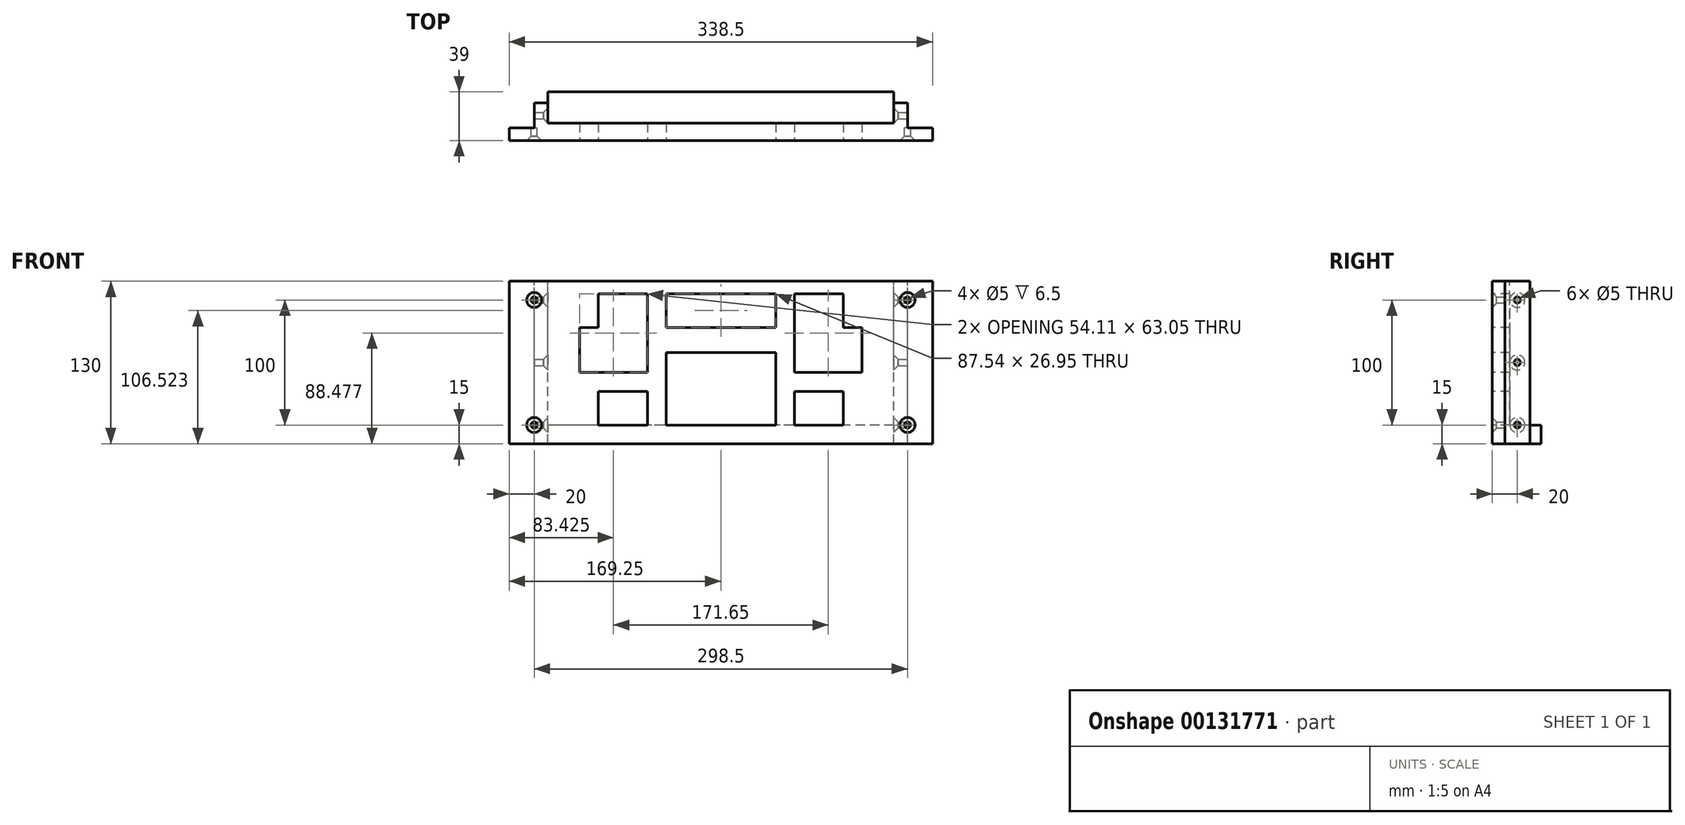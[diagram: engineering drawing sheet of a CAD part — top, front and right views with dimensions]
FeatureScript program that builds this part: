
annotation { "Feature Type Name" : "Feature", "Feature Type Description" : "" }
export const myFeature = defineFeature(function(context is Context, id is Id, definition is map)
    precondition{}
    {
        {
            var Q0;
            Q0=qCreatedBy(makeId("Front.planeOp"),FACE);
            var sketch = newSketch(context, id + "F0", { "sketchPlane" : qUnion([Q0])});
            skLineSegment(sketch, "E0.bottom", {"start": v(0, 0) * mm, "end": v(298.5, 0) * mm});
            skLineSegment(sketch, "E0.top", {"start": v(0, 130) * mm, "end": v(298.5, 130) * mm});
            skLineSegment(sketch, "E0.left", {"start": v(0, 0) * mm, "end": v(0, 130) * mm});
            skLineSegment(sketch, "E0.right", {"start": v(298.5, 0) * mm, "end": v(298.5, 130) * mm});
            skSolve(sketch);
        }
        {
            var Q0;
            Q0=makeQuery(id+"F0.imprint","IMPRINT",FACE,{"disambiguationData":[TD([[makeQuery(id+"F0.imprint","IMPRINT",EDGE,{"derivedFrom":sQuery(id+"F0.wireOp",EDGE,"E0.bottom")}),1.0]])]});
            extrude(context, id + "F1", {"entities" : qUnion([Q0]), "depth" : 14 * mm});
        }
        {
            var Q0;
            Q0=makeQuery(id+"F1.opExtrude","SWEPT_FACE",FACE,{"disambiguationData":[OSD([sQuery(id+"F0.wireOp",EDGE,"E0.top")])]});
            var sketch = newSketch(context, id + "F2", { "sketchPlane" : qUnion([Q0])});
            skLineSegment(sketch, "E1", {"start": v(0, -14) * mm, "end": v(-20, -14) * mm});
            skLineSegment(sketch, "E2", {"start": v(-20, -14) * mm, "end": v(-20, -4) * mm});
            skLineSegment(sketch, "E3", {"start": v(-20, -4) * mm, "end": v(0, -4) * mm});
            skLineSegment(sketch, "E4", {"start": v(0, -4) * mm, "end": v(0, -14) * mm});
            skLineSegment(sketch, "E5.bottom", {"start": v(298.5, -14) * mm, "end": v(318.5, -14) * mm});
            skLineSegment(sketch, "E5.top", {"start": v(298.5, -4) * mm, "end": v(318.5, -4) * mm});
            skLineSegment(sketch, "E5.left", {"start": v(298.5, -14) * mm, "end": v(298.5, -4) * mm});
            skLineSegment(sketch, "E6", {"start": v(318.5, -4) * mm, "end": v(318.5, -14) * mm});
            skSolve(sketch);
        }
        {
            var Q0;
            Q0=makeQuery(id+"F2.imprint","IMPRINT",FACE,{"disambiguationData":[TD([[makeQuery(id+"F2.imprint","IMPRINT",EDGE,{"derivedFrom":sQuery(id+"F2.wireOp",EDGE,"E5.bottom")}),1.0]])]});
            var Q1;
            Q1=makeQuery(id+"F2.imprint","IMPRINT",FACE,{"disambiguationData":[TD([[makeQuery(id+"F2.imprint","IMPRINT",EDGE,{"derivedFrom":sQuery(id+"F2.wireOp",EDGE,"E1")}),-1.0]])]});
            var Q2;
            Q2=makeQuery(id+"F2.imprint","IMPRINT",FACE,{"disambiguationData":[TD([[makeQuery(id+"F2.imprint","IMPRINT",EDGE,{"derivedFrom":sQuery(id+"F2.wireOp",EDGE,"RW2Kzl6v-dZsG-AqaK-MO7M-Wq128sQEg4HD.bottom")}),-1.0]])]});
            var Q3;
            Q3=makeQuery(id+"F1.opExtrude","SWEPT_FACE",FACE,{"disambiguationData":[OSD([sQuery(id+"F0.wireOp",EDGE,"E0.bottom")])]});
            extrude(context, id + "F3", {"entities" : qUnion([Q0, Q1, Q2]), "operationType" : NewBodyOperationType.ADD, "endBound" : BoundingType.UP_TO_SURFACE, "oppositeDirection" : true, "endBoundEntityFace" : qUnion([Q3]), "depth" : 25 * mm});
        }
        {
            var Q0;
            Q0=makeQuery(id+"F3.boolean.opBoolean","MERGE",FACE,{"derivedFrom":[makeQuery(id+"F1.opExtrude","SWEPT_FACE",FACE,{"disambiguationData":[OSD([sQuery(id+"F0.wireOp",EDGE,"E0.top")])]}),makeQuery(id+"F3.opExtrude","CAP_FACE",FACE,{"disambiguationData":[OSD([sQuery(id+"F2.wireOp",EDGE,"E1"),sQuery(id+"F2.wireOp",EDGE,"E2"),sQuery(id+"F2.wireOp",EDGE,"E3"),sQuery(id+"F2.wireOp",EDGE,"E4")])],"isStart":true}),makeQuery(id+"F3.opExtrude","CAP_FACE",FACE,{"disambiguationData":[OSD([sQuery(id+"F2.wireOp",EDGE,"E5.bottom"),sQuery(id+"F2.wireOp",EDGE,"E5.top"),sQuery(id+"F2.wireOp",EDGE,"E5.left"),sQuery(id+"F2.wireOp",EDGE,"E5.right")])],"isStart":true})]});
            var sketch = newSketch(context, id + "F4", { "sketchPlane" : qUnion([Q0])});
            skLineSegment(sketch, "E7", {"start": v(0, 0) * mm, "end": v(0, 16) * mm});
            skLineSegment(sketch, "E8", {"start": v(0, 16) * mm, "end": v(11, 16) * mm});
            skLineSegment(sketch, "E9", {"start": v(11, 16) * mm, "end": v(11, 0) * mm});
            skLineSegment(sketch, "E10", {"start": v(11, 0) * mm, "end": v(0, 0) * mm});
            skLineSegment(sketch, "E11.bottom", {"start": v(298.5, 0) * mm, "end": v(287.5, 0) * mm});
            skLineSegment(sketch, "E11.top", {"start": v(298.5, 16) * mm, "end": v(287.5, 16) * mm});
            skLineSegment(sketch, "E11.left", {"start": v(298.5, 0) * mm, "end": v(298.5, 16) * mm});
            skLineSegment(sketch, "E11.right", {"start": v(287.5, 0) * mm, "end": v(287.5, 16) * mm});
            skSolve(sketch);
        }
        {
            var Q0;
            Q0=makeQuery(id+"F4.imprint","IMPRINT",FACE,{"disambiguationData":[TD([[makeQuery(id+"F4.imprint","IMPRINT",EDGE,{"derivedFrom":sQuery(id+"F4.wireOp",EDGE,"g1681GE8-kr8q-vAWY-LNZA-GesWc0OhcODc.bottom")}),1.0]])]});
            var Q1;
            Q1=makeQuery(id+"F4.imprint","IMPRINT",FACE,{"disambiguationData":[TD([[makeQuery(id+"F4.imprint","IMPRINT",EDGE,{"derivedFrom":sQuery(id+"F4.wireOp",EDGE,"E7")}),-1.0]])]});
            var Q2;
            Q2=makeQuery(id+"F4.imprint","IMPRINT",FACE,{"disambiguationData":[TD([[makeQuery(id+"F4.imprint","IMPRINT",EDGE,{"derivedFrom":sQuery(id+"F4.wireOp",EDGE,"E11.bottom")}),1.0]])]});
            var Q3;
            {var subQ0=sQuery(id+"F0.wireOp",EDGE,"E0.bottom");Q3=makeQuery(id+"F3.boolean.opBoolean","MERGE",FACE,{"derivedFrom":[makeQuery(id+"F1.opExtrude","SWEPT_FACE",FACE,{"disambiguationData":[OSD([subQ0])]}),makeQuery(id+"F3.opExtrude","CAP_FACE",FACE,{"disambiguationData":[OSD([subQ0]),ownerDisambiguation([makeQuery(id+"F3.opExtrude","SWEPT_BODY",BODY,{"disambiguationData":[OSD([sQuery(id+"F2.wireOp",EDGE,"E1"),sQuery(id+"F2.wireOp",EDGE,"E2"),sQuery(id+"F2.wireOp",EDGE,"E3"),sQuery(id+"F2.wireOp",EDGE,"E4")])]})])],"isStart":false}),makeQuery(id+"F3.opExtrude","CAP_FACE",FACE,{"disambiguationData":[OSD([subQ0]),ownerDisambiguation([makeQuery(id+"F3.opExtrude","SWEPT_BODY",BODY,{"disambiguationData":[OSD([sQuery(id+"F2.wireOp",EDGE,"E5.bottom"),sQuery(id+"F2.wireOp",EDGE,"E5.top"),sQuery(id+"F2.wireOp",EDGE,"E5.left"),sQuery(id+"F2.wireOp",EDGE,"E5.right")])]})])],"isStart":false})]});}
            extrude(context, id + "F5", {"entities" : qUnion([Q0, Q1, Q2]), "operationType" : NewBodyOperationType.ADD, "endBound" : BoundingType.UP_TO_SURFACE, "oppositeDirection" : true, "endBoundEntityFace" : qUnion([Q3]), "depth" : 25 * mm});
        }
        {
            var Q0;
            Q0=makeQuery(id+"F3.boolean.opBoolean","MERGE",FACE,{"derivedFrom":[makeQuery(id+"F1.opExtrude","CAP_FACE",FACE,{"disambiguationData":[OSD([sQuery(id+"F0.wireOp",EDGE,"E0.bottom"),sQuery(id+"F0.wireOp",EDGE,"E0.top"),sQuery(id+"F0.wireOp",EDGE,"E0.left"),sQuery(id+"F0.wireOp",EDGE,"E0.right")])],"isStart":false}),makeQuery(id+"F3.opExtrude","SWEPT_FACE",FACE,{"disambiguationData":[OSD([sQuery(id+"F2.wireOp",EDGE,"E1")])]}),makeQuery(id+"F3.opExtrude","SWEPT_FACE",FACE,{"disambiguationData":[OSD([sQuery(id+"F2.wireOp",EDGE,"E5.bottom")])]})]});
            var sketch = newSketch(context, id + "F6", { "sketchPlane" : qUnion([Q0])});
            skLineSegment(sketch, "E12.0", {"start": v(51.37, 93.05) * mm, "end": v(51.37, 120) * mm});
            skLineSegment(sketch, "E12.6", {"start": v(51.37, 120) * mm, "end": v(247.13, 120) * mm});
            skLineSegment(sketch, "E12.8", {"start": v(51.37, 15) * mm, "end": v(51.37, 41.95) * mm});
            skLineSegment(sketch, "E12.11", {"start": v(36.37, 93.05) * mm, "end": v(51.37, 93.05) * mm});
            skLineSegment(sketch, "E13", {"start": v(149.25, 120) * mm, "end": v(149.25, 15) * mm});
            skLineSegment(sketch, "E14", {"start": v(51.37, 15) * mm, "end": v(149.25, 120) * mm, "construction": true});
            skLineSegment(sketch, "E15", {"start": v(149.25, 120) * mm, "end": v(247.13, 15) * mm, "construction": true});
            skLineSegment(sketch, "E16.bottom", {"start": v(105.48, 73.05) * mm, "end": v(193.02, 73.05) * mm});
            skLineSegment(sketch, "E16.top", {"start": v(105.48, 15) * mm, "end": v(193.02, 15) * mm});
            skLineSegment(sketch, "E16.left", {"start": v(105.48, 73.05) * mm, "end": v(105.48, 15) * mm});
            skLineSegment(sketch, "E16.right", {"start": v(193.02, 73.05) * mm, "end": v(193.02, 15) * mm});
            skLineSegment(sketch, "E17.bottom", {"start": v(262.13, 56.95) * mm, "end": v(208.02, 56.95) * mm});
            skLineSegment(sketch, "E17.right", {"start": v(208.02, 56.95) * mm, "end": v(208.02, 120) * mm});
            skLineSegment(sketch, "E18.bottom", {"start": v(90.48, 120) * mm, "end": v(51.37, 120) * mm});
            skLineSegment(sketch, "E18.top", {"start": v(90.48, 56.95) * mm, "end": v(36.37, 56.95) * mm});
            skLineSegment(sketch, "E18.left", {"start": v(90.48, 120) * mm, "end": v(90.48, 56.95) * mm});
            skLineSegment(sketch, "E18.right", {"start": v(51.37, 120) * mm, "end": v(51.37, 93.05) * mm});
            skLineSegment(sketch, "E19.bottom", {"start": v(105.48, 120) * mm, "end": v(193.02, 120) * mm});
            skLineSegment(sketch, "E19.top", {"start": v(105.48, 93.05) * mm, "end": v(193.02, 93.05) * mm});
            skLineSegment(sketch, "E19.left", {"start": v(105.48, 120) * mm, "end": v(105.48, 93.05) * mm});
            skLineSegment(sketch, "E19.right", {"start": v(193.02, 120) * mm, "end": v(193.02, 93.05) * mm});
            skLineSegment(sketch, "E20.bottom", {"start": v(208.02, 15) * mm, "end": v(247.13, 15) * mm});
            skLineSegment(sketch, "E20.top", {"start": v(208.02, 41.95) * mm, "end": v(247.13, 41.95) * mm});
            skLineSegment(sketch, "E20.left", {"start": v(208.02, 15) * mm, "end": v(208.02, 41.95) * mm});
            skLineSegment(sketch, "E21.bottom", {"start": v(51.37, 15) * mm, "end": v(90.48, 15) * mm});
            skLineSegment(sketch, "E21.top", {"start": v(51.37, 41.95) * mm, "end": v(90.48, 41.95) * mm});
            skLineSegment(sketch, "E21.right", {"start": v(90.48, 15) * mm, "end": v(90.48, 41.95) * mm});
            skLineSegment(sketch, "E22", {"start": v(36.37, 93.05) * mm, "end": v(36.37, 56.95) * mm});
            skLineSegment(sketch, "E23.trimOffspring", {"start": v(247.13, 15) * mm, "end": v(51.37, 15) * mm});
            skLineSegment(sketch, "E24.trimOffspring", {"start": v(247.13, 120) * mm, "end": v(208.02, 120) * mm});
            skLineSegment(sketch, "E25.0", {"start": v(11, 0) * mm, "end": v(11, 130) * mm});
            skLineSegment(sketch, "E26.0", {"start": v(287.5, 0) * mm, "end": v(287.5, 130) * mm});
            skLineSegment(sketch, "E27", {"start": v(11, 15) * mm, "end": v(90.48, 15) * mm});
            skLineSegment(sketch, "E28", {"start": v(247.13, 93.05) * mm, "end": v(262.13, 93.05) * mm});
            skPoint(sketch, "E28.startSnap0", {"position": v(149.25, 93.05) * mm});
            skLineSegment(sketch, "E29", {"start": v(262.13, 93.05) * mm, "end": v(262.13, 56.95) * mm});
            skLineSegment(sketch, "E30", {"start": v(247.13, 93.05) * mm, "end": v(247.13, 120) * mm});
            skLineSegment(sketch, "E31", {"start": v(247.13, 41.95) * mm, "end": v(247.13, 15) * mm});
            skLineSegment(sketch, "E32.trimOffspring", {"start": v(149.25, 15) * mm, "end": v(287.5, 15) * mm});
            skSolve(sketch);
        }
        {
            var Q0;
            {var subQ0=sQuery(id+"F6.wireOp",EDGE,"E12.11");Q0=makeQuery(id+"F6.imprint","IMPRINT",FACE,{"disambiguationData":[TD([[makeQuery(id+"F6.imprint","IMPRINT",EDGE,{"derivedFrom":subQ0}),-1.0]])]});}
            var Q1;
            Q1=makeQuery(id+"F6.imprint","IMPRINT",FACE,{"disambiguationData":[TD([[makeQuery(id+"F6.imprint","IMPRINT",EDGE,{"derivedFrom":sQuery(id+"F6.wireOp",EDGE,"E21.bottom")}),1.0]])]});
            var Q2;
            {var subQ5=sQuery(id+"F6.wireOp",EDGE,"E16.left");Q2=makeQuery(id+"F6.imprint","IMPRINT",FACE,{"disambiguationData":[TD([[makeQuery(id+"F6.imprint","IMPRINT",EDGE,{"derivedFrom":subQ5}),1.0]])]});}
            var Q3;
            {var subQ5=sQuery(id+"F6.wireOp",EDGE,"E16.right");Q3=makeQuery(id+"F6.imprint","IMPRINT",FACE,{"disambiguationData":[TD([[makeQuery(id+"F6.imprint","IMPRINT",EDGE,{"derivedFrom":subQ5}),-1.0]])]});}
            var Q4;
            {var subQ5=sQuery(id+"F6.wireOp",EDGE,"E19.left");Q4=makeQuery(id+"F6.imprint","IMPRINT",FACE,{"disambiguationData":[TD([[makeQuery(id+"F6.imprint","IMPRINT",EDGE,{"derivedFrom":subQ5}),1.0]])]});}
            var Q5;
            {var subQ5=sQuery(id+"F6.wireOp",EDGE,"E19.right");Q5=makeQuery(id+"F6.imprint","IMPRINT",FACE,{"disambiguationData":[TD([[makeQuery(id+"F6.imprint","IMPRINT",EDGE,{"derivedFrom":subQ5}),-1.0]])]});}
            var Q6;
            {var subQ5=sQuery(id+"F6.wireOp",EDGE,"E17.right");Q6=makeQuery(id+"F6.imprint","IMPRINT",FACE,{"disambiguationData":[TD([[makeQuery(id+"F6.imprint","IMPRINT",EDGE,{"derivedFrom":subQ5}),-1.0]])]});}
            var Q7;
            {var subQ5=sQuery(id+"F6.wireOp",EDGE,"E17.left");Q7=makeQuery(id+"F6.imprint","IMPRINT",FACE,{"disambiguationData":[TD([[makeQuery(id+"F6.imprint","IMPRINT",EDGE,{"derivedFrom":subQ5}),1.0]])]});}
            var Q8;
            {var subQ5=sQuery(id+"F6.wireOp",EDGE,"E20.left");Q8=makeQuery(id+"F6.imprint","IMPRINT",FACE,{"disambiguationData":[TD([[makeQuery(id+"F6.imprint","IMPRINT",EDGE,{"derivedFrom":subQ5}),-1.0]])]});}
            var Q9;
            {var subQ5=sQuery(id+"F6.wireOp",EDGE,"E20.right");Q9=makeQuery(id+"F6.imprint","IMPRINT",FACE,{"disambiguationData":[TD([[makeQuery(id+"F6.imprint","IMPRINT",EDGE,{"derivedFrom":subQ5}),1.0]])]});}
            var Q10;
            {var subQ5=sQuery(id+"F6.wireOp",EDGE,"hvbMsxLx-pQPf-gS8o-dKST-O0hyGc2vKU4P.left");Q10=makeQuery(id+"F6.imprint","IMPRINT",FACE,{"disambiguationData":[TD([[makeQuery(id+"F6.imprint","IMPRINT",EDGE,{"derivedFrom":subQ5}),1.0]])]});}
            var Q11;
            {var subQ5=sQuery(id+"F6.wireOp",EDGE,"hvbMsxLx-pQPf-gS8o-dKST-O0hyGc2vKU4P.right");Q11=makeQuery(id+"F6.imprint","IMPRINT",FACE,{"disambiguationData":[TD([[makeQuery(id+"F6.imprint","IMPRINT",EDGE,{"derivedFrom":subQ5}),-1.0]])]});}
            var Q12;
            {var subQ5=sQuery(id+"F6.wireOp",EDGE,"HBe9uRum-s8Nd-G8Iq-C5LE-OKOHOuB29JyI.right");Q12=makeQuery(id+"F6.imprint","IMPRINT",FACE,{"disambiguationData":[TD([[makeQuery(id+"F6.imprint","IMPRINT",EDGE,{"derivedFrom":subQ5}),-1.0]])]});}
            var Q13;
            {var subQ5=sQuery(id+"F6.wireOp",EDGE,"HBe9uRum-s8Nd-G8Iq-C5LE-OKOHOuB29JyI.left");Q13=makeQuery(id+"F6.imprint","IMPRINT",FACE,{"disambiguationData":[TD([[makeQuery(id+"F6.imprint","IMPRINT",EDGE,{"derivedFrom":subQ5}),1.0]])]});}
            var Q14;
            {var subQ0=sQuery(id+"F6.wireOp",EDGE,"E12.3");Q14=makeQuery(id+"F6.imprint","IMPRINT",FACE,{"disambiguationData":[TD([[makeQuery(id+"F6.imprint","IMPRINT",EDGE,{"derivedFrom":subQ0}),-1.0]])]});}
            var Q15;
            Q15=makeQuery(id+"F6.imprint","IMPRINT",FACE,{"disambiguationData":[TD([[makeQuery(id+"F6.imprint","IMPRINT",EDGE,{"derivedFrom":sQuery(id+"F6.wireOp",EDGE,"QVOU0Kov-pEP3-pyCc-9Jsp-ffBmEvdx701M.bottom")}),-1.0]])]});
            var Q16;
            Q16=makeQuery(id+"F6.imprint","IMPRINT",FACE,{"disambiguationData":[TD([[makeQuery(id+"F6.imprint","IMPRINT",EDGE,{"derivedFrom":sQuery(id+"F6.wireOp",EDGE,"E21.top")}),-1.0]])]});
            extrude(context, id + "F7", {"entities" : qUnion([Q0, Q1, Q2, Q3, Q4, Q5, Q6, Q7, Q8, Q9, Q10, Q11, Q12, Q13, Q14, Q15, Q16]), "operationType" : NewBodyOperationType.REMOVE, "oppositeDirection" : true, "depth" : 25 * mm});
        }
        {
            var Q0;
            Q0=makeQuery(id+"F3.opExtrude","SWEPT_FACE",FACE,{"disambiguationData":[OSD([sQuery(id+"F2.wireOp",EDGE,"E5.top")])]});
            var sketch = newSketch(context, id + "F8", { "sketchPlane" : qUnion([Q0])});
            skCircle(sketch, "E33", {"center": v(-298.5, 115) * mm, "radius": 2.5 * mm});
            skCircle(sketch, "E34", {"center": v(-298.5, 15) * mm, "radius": 2.5 * mm});
            skCircle(sketch, "E35", {"center": v(0, 115) * mm, "radius": 2.5 * mm});
            skCircle(sketch, "E36", {"center": v(0, 15) * mm, "radius": 2.5 * mm});
            skLineSegment(sketch, "E37.bottom", {"start": v(-298.5, 115) * mm, "end": v(0, 115) * mm, "construction": true});
            skLineSegment(sketch, "E37.top", {"start": v(-298.5, 15) * mm, "end": v(0, 15) * mm, "construction": true});
            skLineSegment(sketch, "E37.left", {"start": v(-298.5, 115) * mm, "end": v(-298.5, 15) * mm, "construction": true});
            skLineSegment(sketch, "E37.right", {"start": v(0, 115) * mm, "end": v(0, 15) * mm, "construction": true});
            skSolve(sketch);
        }
        {
            var Q0;
            Q0=qSketchRegion(id+"F8",true);
            extrude(context, id + "F9", {"entities" : qUnion([Q0]), "operationType" : NewBodyOperationType.REMOVE, "oppositeDirection" : true, "depth" : 25 * mm});
        }
        {
            var Q0;
            Q0=makeQuery(id+"F5.boolean.opBoolean","MERGE",FACE,{"derivedFrom":[makeQuery(id+"F1.opExtrude","SWEPT_FACE",FACE,{"disambiguationData":[OSD([sQuery(id+"F0.wireOp",EDGE,"E0.right")])]}),makeQuery(id+"F5.opExtrude","SWEPT_FACE",FACE,{"disambiguationData":[OSD([sQuery(id+"F4.wireOp",EDGE,"E11.left")])]})]});
            var sketch = newSketch(context, id + "F10", { "sketchPlane" : qUnion([Q0])});
            skCircle(sketch, "E38", {"center": v(6, 115) * mm, "radius": 2.5 * mm});
            skCircle(sketch, "E39", {"center": v(6, 15) * mm, "radius": 2.5 * mm});
            skCircle(sketch, "E40", {"center": v(6, 65) * mm, "radius": 2.5 * mm});
            skSolve(sketch);
        }
        {
            var Q0;
            Q0=qSketchRegion(id+"F10",true);
            extrude(context, id + "F11", {"entities" : qUnion([Q0]), "operationType" : NewBodyOperationType.REMOVE, "endBound" : BoundingType.THROUGH_ALL, "oppositeDirection" : true, "depth" : 25 * mm});
        }
        {
            var Q0;
            Q0=makeQuery(id+"F9.boolean.opBoolean","INTERSECT",EDGE,{"derivedFrom":[makeQuery(id+"F3.boolean.opBoolean","MERGE",FACE,{"derivedFrom":[makeQuery(id+"F1.opExtrude","CAP_FACE",FACE,{"disambiguationData":[OSD([sQuery(id+"F0.wireOp",EDGE,"E0.bottom"),sQuery(id+"F0.wireOp",EDGE,"E0.top"),sQuery(id+"F0.wireOp",EDGE,"E0.left"),sQuery(id+"F0.wireOp",EDGE,"E0.right")])],"isStart":false}),makeQuery(id+"F3.opExtrude","SWEPT_FACE",FACE,{"disambiguationData":[OSD([sQuery(id+"F2.wireOp",EDGE,"E1")])]}),makeQuery(id+"F3.opExtrude","SWEPT_FACE",FACE,{"disambiguationData":[OSD([sQuery(id+"F2.wireOp",EDGE,"E5.bottom")])]})]}),makeQuery(id+"F9.opExtrude","SWEPT_FACE",FACE,{"disambiguationData":[OSD([sQuery(id+"F8.wireOp",EDGE,"E33")])]})]});
            var Q1;
            Q1=makeQuery(id+"F9.boolean.opBoolean","INTERSECT",EDGE,{"derivedFrom":[makeQuery(id+"F3.boolean.opBoolean","MERGE",FACE,{"derivedFrom":[makeQuery(id+"F1.opExtrude","CAP_FACE",FACE,{"disambiguationData":[OSD([sQuery(id+"F0.wireOp",EDGE,"E0.bottom"),sQuery(id+"F0.wireOp",EDGE,"E0.top"),sQuery(id+"F0.wireOp",EDGE,"E0.left"),sQuery(id+"F0.wireOp",EDGE,"E0.right")])],"isStart":false}),makeQuery(id+"F3.opExtrude","SWEPT_FACE",FACE,{"disambiguationData":[OSD([sQuery(id+"F2.wireOp",EDGE,"E1")])]}),makeQuery(id+"F3.opExtrude","SWEPT_FACE",FACE,{"disambiguationData":[OSD([sQuery(id+"F2.wireOp",EDGE,"E5.bottom")])]})]}),makeQuery(id+"F9.opExtrude","SWEPT_FACE",FACE,{"disambiguationData":[OSD([sQuery(id+"F8.wireOp",EDGE,"E34")])]})]});
            var Q2;
            Q2=makeQuery(id+"F9.boolean.opBoolean","INTERSECT",EDGE,{"derivedFrom":[makeQuery(id+"F3.boolean.opBoolean","MERGE",FACE,{"derivedFrom":[makeQuery(id+"F1.opExtrude","CAP_FACE",FACE,{"disambiguationData":[OSD([sQuery(id+"F0.wireOp",EDGE,"E0.bottom"),sQuery(id+"F0.wireOp",EDGE,"E0.top"),sQuery(id+"F0.wireOp",EDGE,"E0.left"),sQuery(id+"F0.wireOp",EDGE,"E0.right")])],"isStart":false}),makeQuery(id+"F3.opExtrude","SWEPT_FACE",FACE,{"disambiguationData":[OSD([sQuery(id+"F2.wireOp",EDGE,"E1")])]}),makeQuery(id+"F3.opExtrude","SWEPT_FACE",FACE,{"disambiguationData":[OSD([sQuery(id+"F2.wireOp",EDGE,"E5.bottom")])]})]}),makeQuery(id+"F9.opExtrude","SWEPT_FACE",FACE,{"disambiguationData":[OSD([sQuery(id+"F8.wireOp",EDGE,"E35")])]})]});
            var Q3;
            Q3=makeQuery(id+"F9.boolean.opBoolean","INTERSECT",EDGE,{"derivedFrom":[makeQuery(id+"F3.boolean.opBoolean","MERGE",FACE,{"derivedFrom":[makeQuery(id+"F1.opExtrude","CAP_FACE",FACE,{"disambiguationData":[OSD([sQuery(id+"F0.wireOp",EDGE,"E0.bottom"),sQuery(id+"F0.wireOp",EDGE,"E0.top"),sQuery(id+"F0.wireOp",EDGE,"E0.left"),sQuery(id+"F0.wireOp",EDGE,"E0.right")])],"isStart":false}),makeQuery(id+"F3.opExtrude","SWEPT_FACE",FACE,{"disambiguationData":[OSD([sQuery(id+"F2.wireOp",EDGE,"E1")])]}),makeQuery(id+"F3.opExtrude","SWEPT_FACE",FACE,{"disambiguationData":[OSD([sQuery(id+"F2.wireOp",EDGE,"E5.bottom")])]})]}),makeQuery(id+"F9.opExtrude","SWEPT_FACE",FACE,{"disambiguationData":[OSD([sQuery(id+"F8.wireOp",EDGE,"E36")])]})]});
            var Q4;
            Q4=makeQuery(id+"F11.boolean.opBoolean","INTERSECT",EDGE,{"derivedFrom":[makeQuery(id+"F5.opExtrude","SWEPT_FACE",FACE,{"disambiguationData":[OSD([sQuery(id+"F4.wireOp",EDGE,"E11.right")])]}),makeQuery(id+"F11.opExtrude","SWEPT_FACE",FACE,{"disambiguationData":[OSD([sQuery(id+"F10.wireOp",EDGE,"E38")])]})]});
            var Q5;
            Q5=makeQuery(id+"F11.boolean.opBoolean","INTERSECT",EDGE,{"derivedFrom":[makeQuery(id+"F5.opExtrude","SWEPT_FACE",FACE,{"disambiguationData":[OSD([sQuery(id+"F4.wireOp",EDGE,"E11.right")])]}),makeQuery(id+"F11.opExtrude","SWEPT_FACE",FACE,{"disambiguationData":[OSD([sQuery(id+"F10.wireOp",EDGE,"E40")])]})]});
            var Q6;
            Q6=makeQuery(id+"F11.boolean.opBoolean","INTERSECT",EDGE,{"derivedFrom":[makeQuery(id+"F5.opExtrude","SWEPT_FACE",FACE,{"disambiguationData":[OSD([sQuery(id+"F4.wireOp",EDGE,"E11.right")])]}),makeQuery(id+"F11.opExtrude","SWEPT_FACE",FACE,{"disambiguationData":[OSD([sQuery(id+"F10.wireOp",EDGE,"E39")])]})]});
            var Q7;
            Q7=makeQuery(id+"F11.boolean.opBoolean","INTERSECT",EDGE,{"derivedFrom":[makeQuery(id+"F5.opExtrude","SWEPT_FACE",FACE,{"disambiguationData":[OSD([sQuery(id+"F4.wireOp",EDGE,"E9")])]}),makeQuery(id+"F11.opExtrude","SWEPT_FACE",FACE,{"disambiguationData":[OSD([sQuery(id+"F10.wireOp",EDGE,"E38")])]})]});
            var Q8;
            Q8=makeQuery(id+"F11.boolean.opBoolean","INTERSECT",EDGE,{"derivedFrom":[makeQuery(id+"F5.opExtrude","SWEPT_FACE",FACE,{"disambiguationData":[OSD([sQuery(id+"F4.wireOp",EDGE,"E9")])]}),makeQuery(id+"F11.opExtrude","SWEPT_FACE",FACE,{"disambiguationData":[OSD([sQuery(id+"F10.wireOp",EDGE,"E40")])]})]});
            var Q9;
            Q9=makeQuery(id+"F11.boolean.opBoolean","INTERSECT",EDGE,{"derivedFrom":[makeQuery(id+"F5.opExtrude","SWEPT_FACE",FACE,{"disambiguationData":[OSD([sQuery(id+"F4.wireOp",EDGE,"E9")])]}),makeQuery(id+"F11.opExtrude","SWEPT_FACE",FACE,{"disambiguationData":[OSD([sQuery(id+"F10.wireOp",EDGE,"E39")])]})]});
            chamfer(context, id + "F12", {"entities" : qUnion([Q0, Q1, Q2, Q3, Q4, Q5, Q6, Q7, Q8, Q9]), "width" : 3.5 * mm, "tangentPropagation" : true});
        }
        {
            var Q0;
            Q0=makeQuery(id+"F1.opExtrude","CAP_FACE",FACE,{"disambiguationData":[OSD([sQuery(id+"F0.wireOp",EDGE,"E0.bottom"),sQuery(id+"F0.wireOp",EDGE,"E0.top"),sQuery(id+"F0.wireOp",EDGE,"E0.left"),sQuery(id+"F0.wireOp",EDGE,"E0.right")])],"isStart":true});
            var sketch = newSketch(context, id + "F14", { "sketchPlane" : qUnion([Q0])});
            skLineSegment(sketch, "E41.0", {"start": v(-287.5, 0) * mm, "end": v(-287.5, 15) * mm});
            skLineSegment(sketch, "E42.0", {"start": v(-11, 0) * mm, "end": v(-11, 15) * mm});
            skLineSegment(sketch, "E43", {"start": v(-287.5, 15) * mm, "end": v(-11, 15) * mm});
            skPoint(sketch, "E43.endSnap0", {"position": v(-11, 7.5) * mm});
            skLineSegment(sketch, "E44.0", {"start": v(-11, 0) * mm, "end": v(-287.5, 0) * mm});
            skSolve(sketch);
        }
        {
            var Q0;
            Q0 = qSketchRegion(id + "F14", true);
            extrude(context, id + "F13", {"entities" : qUnion([Q0]), "operationType" : NewBodyOperationType.ADD, "depth" : 25 * mm});
        }
    });
